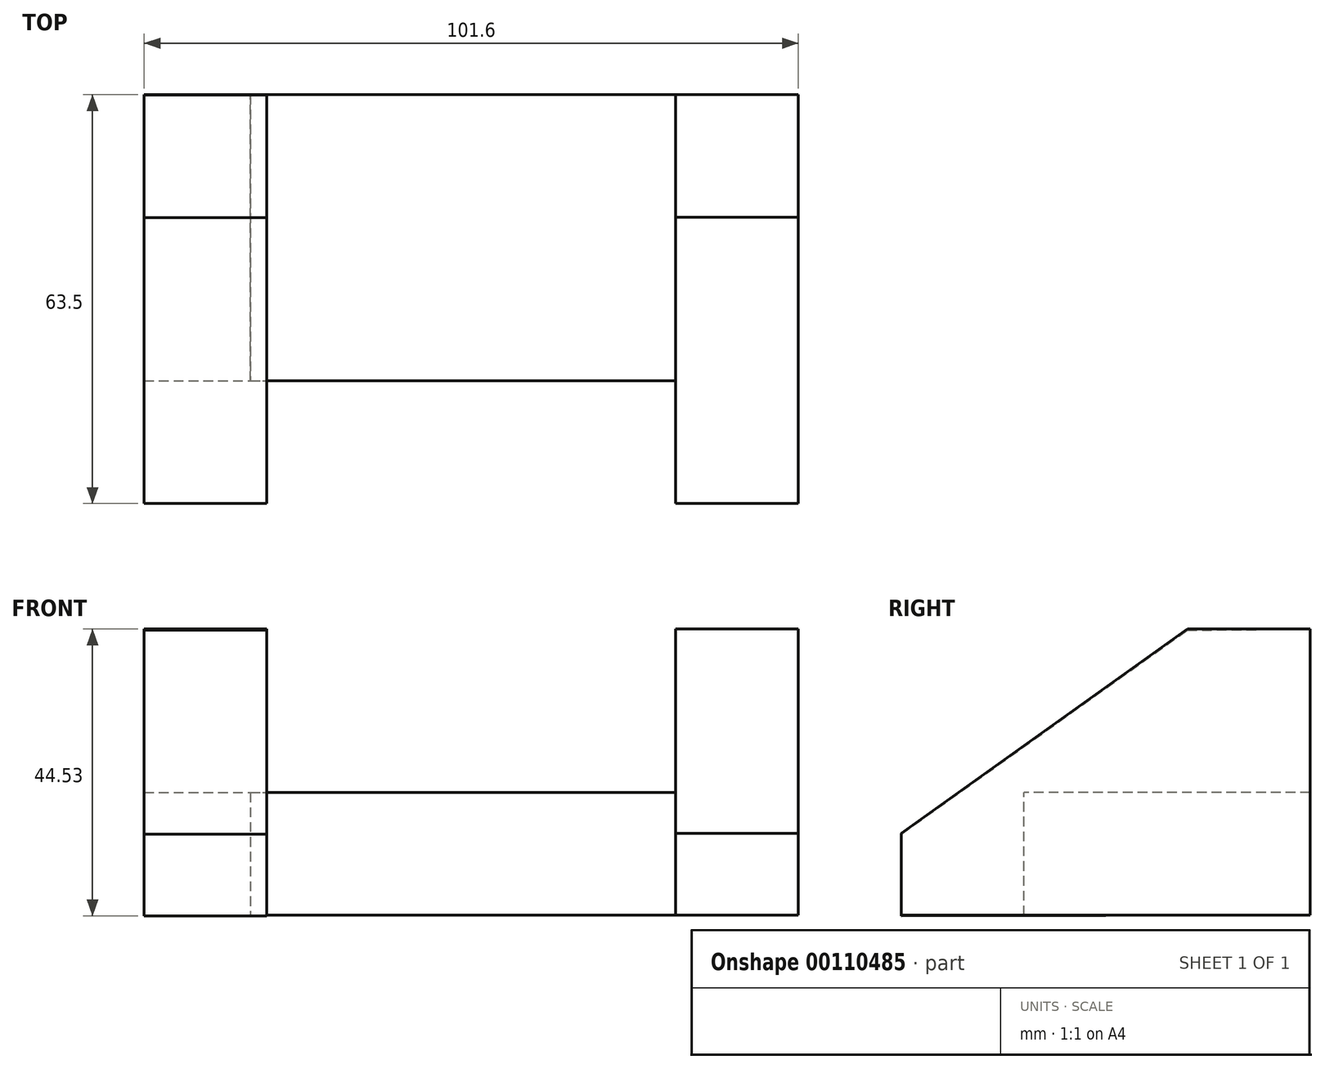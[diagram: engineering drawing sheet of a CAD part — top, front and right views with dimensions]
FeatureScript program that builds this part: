
annotation { "Feature Type Name" : "Feature", "Feature Type Description" : "" }
export const myFeature = defineFeature(function(context is Context, id is Id, definition is map)
    precondition{}
    {
        {
            var Q0;
            Q0=qCreatedBy(makeId("Right.planeOp"),FACE);
            var sketch = newSketch(context, id + "F0", { "sketchPlane" : qUnion([Q0])});
            skLineSegment(sketch, "E0", {"start": v(-25.66, -8.92) * mm, "end": v(-25.66, -21.62) * mm});
            skLineSegment(sketch, "E1", {"start": v(-25.66, -21.62) * mm, "end": v(37.84, -21.62) * mm});
            skLineSegment(sketch, "E2", {"start": v(37.84, -21.62) * mm, "end": v(37.84, 22.83) * mm});
            skLineSegment(sketch, "E3", {"start": v(37.84, 22.83) * mm, "end": v(18.8, 22.83) * mm});
            skLineSegment(sketch, "E4", {"start": v(18.8, 22.83) * mm, "end": v(-25.66, -8.92) * mm});
            skSolve(sketch);
        }
        {
            var Q0;
            Q0=makeQuery(id+"F0.imprint","IMPRINT",FACE,{"disambiguationData":[TD([[makeQuery(id+"F0.imprint","IMPRINT",EDGE,{"derivedFrom":sQuery(id+"F0.wireOp",EDGE,"E0")}),1.0]])]});
            extrude(context, id + "F1", {"entities" : qUnion([Q0]), "depth" : 19.05 * mm});
        }
        {
            var Q0;
            Q0=makeQuery(id+"F1.opExtrude","CAP_FACE",FACE,{"disambiguationData":[OSD([sQuery(id+"F0.wireOp",EDGE,"E0"),sQuery(id+"F0.wireOp",EDGE,"E1"),sQuery(id+"F0.wireOp",EDGE,"E2"),sQuery(id+"F0.wireOp",EDGE,"E3"),sQuery(id+"F0.wireOp",EDGE,"E4")])],"isStart":true});
            var sketch = newSketch(context, id + "F2", { "sketchPlane" : qUnion([Q0])});
            skLineSegment(sketch, "E5", {"start": v(-37.84, -21.62) * mm, "end": v(-37.84, -2.57) * mm});
            skLineSegment(sketch, "E6", {"start": v(-37.84, -21.62) * mm, "end": v(6.6, -21.62) * mm});
            skLineSegment(sketch, "E7", {"start": v(6.6, -21.62) * mm, "end": v(6.6, -2.57) * mm});
            skLineSegment(sketch, "E8", {"start": v(-37.84, -2.57) * mm, "end": v(6.6, -2.57) * mm});
            skSolve(sketch);
        }
        {
            var Q0;
            Q0=makeQuery(id+"F2.imprint","IMPRINT",FACE,{"disambiguationData":[TD([[makeQuery(id+"F2.imprint","IMPRINT",EDGE,{"derivedFrom":sQuery(id+"F2.wireOp",EDGE,"E5")}),-1.0]])]});
            extrude(context, id + "F3", {"entities" : qUnion([Q0]), "operationType" : NewBodyOperationType.ADD, "depth" : 63.5 * mm});
        }
        {
            var Q0;
            Q0=makeQuery(id+"F3.opExtrude","CAP_FACE",FACE,{"disambiguationData":[OSD([sQuery(id+"F2.wireOp",EDGE,"E5"),sQuery(id+"F2.wireOp",EDGE,"E6"),sQuery(id+"F2.wireOp",EDGE,"E7"),sQuery(id+"F2.wireOp",EDGE,"E8")])],"isStart":false});
            var sketch = newSketch(context, id + "F4", { "sketchPlane" : qUnion([Q0])});
            skLineSegment(sketch, "E9", {"start": v(-37.79, 22.83) * mm, "end": v(-37.84, -21.62) * mm});
            skLineSegment(sketch, "E10", {"start": v(-37.84, -21.62) * mm, "end": v(25.66, -21.7) * mm});
            skLineSegment(sketch, "E11", {"start": v(25.66, -21.7) * mm, "end": v(25.66, -9) * mm});
            skLineSegment(sketch, "E12", {"start": v(25.66, -9) * mm, "end": v(-18.74, 22.65) * mm});
            skLineSegment(sketch, "E13", {"start": v(-18.74, 22.65) * mm, "end": v(-37.79, 22.83) * mm});
            skSolve(sketch);
        }
        {
            var Q0;
            Q0=makeQuery(id+"F4.imprint","IMPRINT",FACE,{"disambiguationData":[TD([[makeQuery(id+"F4.imprint","IMPRINT",EDGE,{"derivedFrom":sQuery(id+"F4.wireOp",EDGE,"EcuD0eLd-g7NP-chcj-YMvJ-MnP9BEGNGOha")}),-1.0]])]});
            var Q1;
            Q1=makeQuery(id+"F4.imprint","IMPRINT",FACE,{"disambiguationData":[TD([[makeQuery(id+"F4.imprint","IMPRINT",EDGE,{"derivedFrom":sQuery(id+"F4.wireOp",EDGE,"E10")}),1.0]])]});
            extrude(context, id + "F5", {"entities" : qUnion([Q0, Q1]), "operationType" : NewBodyOperationType.ADD, "depth" : 19.05 * mm});
        }
        {
            var Q0;
            {var subQ1=makeQuery(id+"F3.opExtrude","CAP_EDGE",EDGE,{"disambiguationData":[OSD([sQuery(id+"F2.wireOp",EDGE,"E6")])],"isStart":false});Q0=makeQuery(id+"F4.imprint","IMPRINT",FACE,{"disambiguationData":[TD([[makeQuery(id+"F4.imprint","IMPRINT",EDGE,{"derivedFrom":subQ1}),-1.0]])]});}
            extrude(context, id + "F6", {"entities" : qUnion([Q0]), "depth" : 2.54 * mm});
        }
    });
